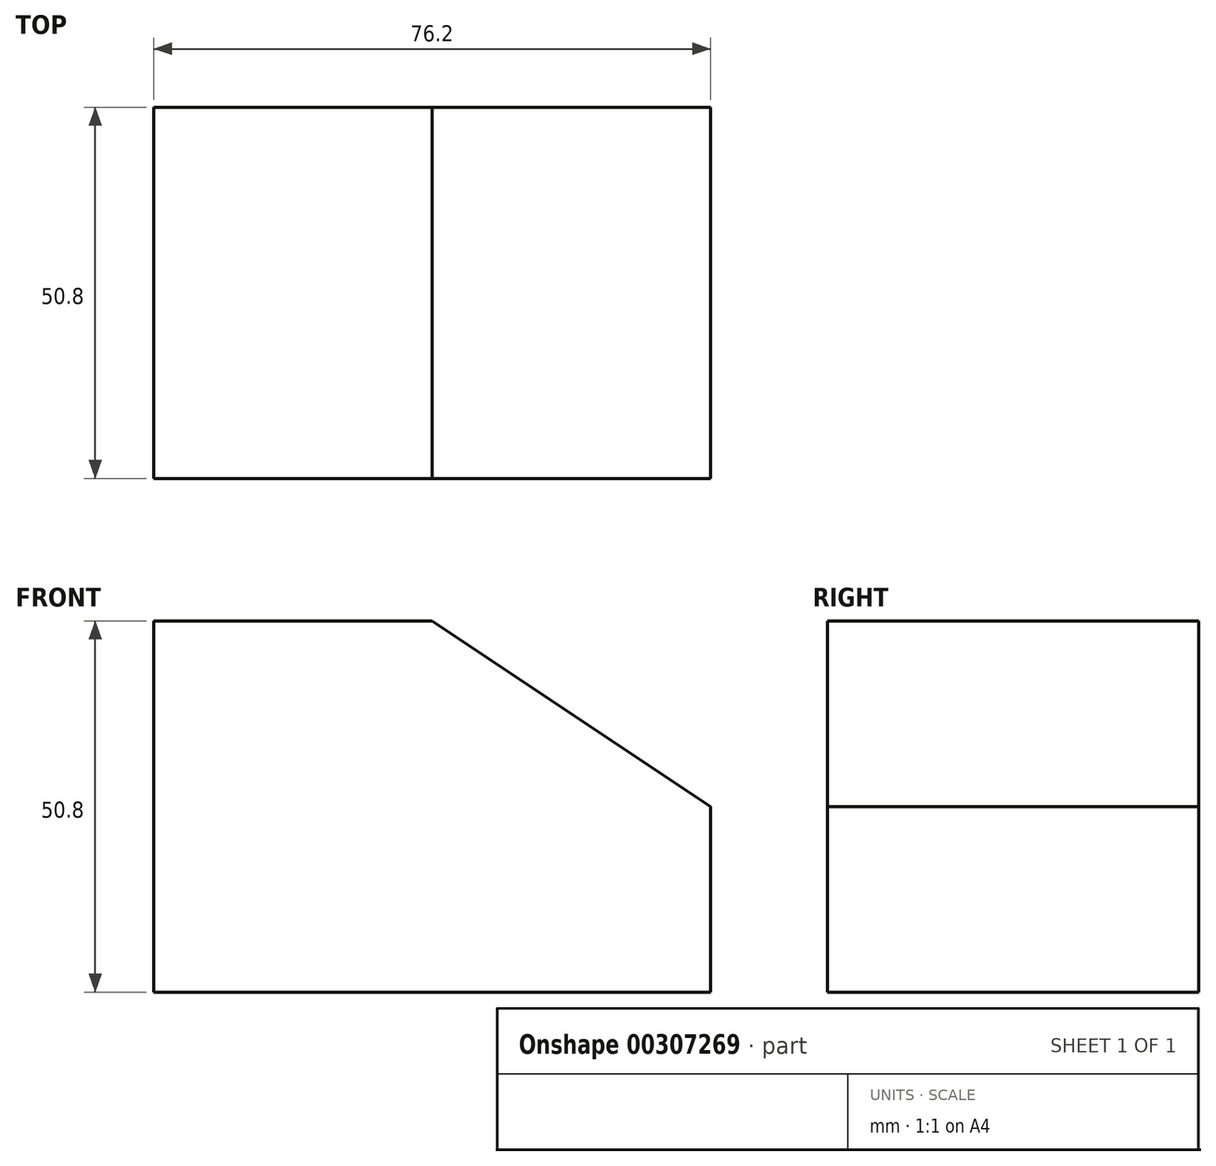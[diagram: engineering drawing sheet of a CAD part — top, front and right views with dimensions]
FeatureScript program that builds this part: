
annotation { "Feature Type Name" : "Feature", "Feature Type Description" : "" }
export const myFeature = defineFeature(function(context is Context, id is Id, definition is map)
    precondition{}
    {
        {
            var Q0;
            Q0=qCreatedBy(makeId("Front.planeOp"),FACE);
            var sketch = newSketch(context, id + "F0", { "sketchPlane" : qUnion([Q0])});
            skLineSegment(sketch, "E0", {"start": v(-48.93, 25.64) * mm, "end": v(-48.93, -25.16) * mm});
            skLineSegment(sketch, "E1", {"start": v(-48.93, -25.16) * mm, "end": v(27.27, -25.16) * mm});
            skLineSegment(sketch, "E2", {"start": v(27.27, -25.16) * mm, "end": v(27.27, 0.24) * mm});
            skLineSegment(sketch, "E3", {"start": v(27.27, 0.24) * mm, "end": v(-10.83, 25.64) * mm});
            skLineSegment(sketch, "E4", {"start": v(-10.83, 25.64) * mm, "end": v(-48.93, 25.64) * mm});
            skSolve(sketch);
        }
        {
            var Q0;
            Q0=makeQuery(id+"F0.imprint","IMPRINT",FACE,{"disambiguationData":[TD([[makeQuery(id+"F0.imprint","IMPRINT",EDGE,{"derivedFrom":sQuery(id+"F0.wireOp",EDGE,"E0")}),1.0]])]});
            extrude(context, id + "F1", {"entities" : qUnion([Q0]), "depth" : 50.8 * mm});
        }
    });
